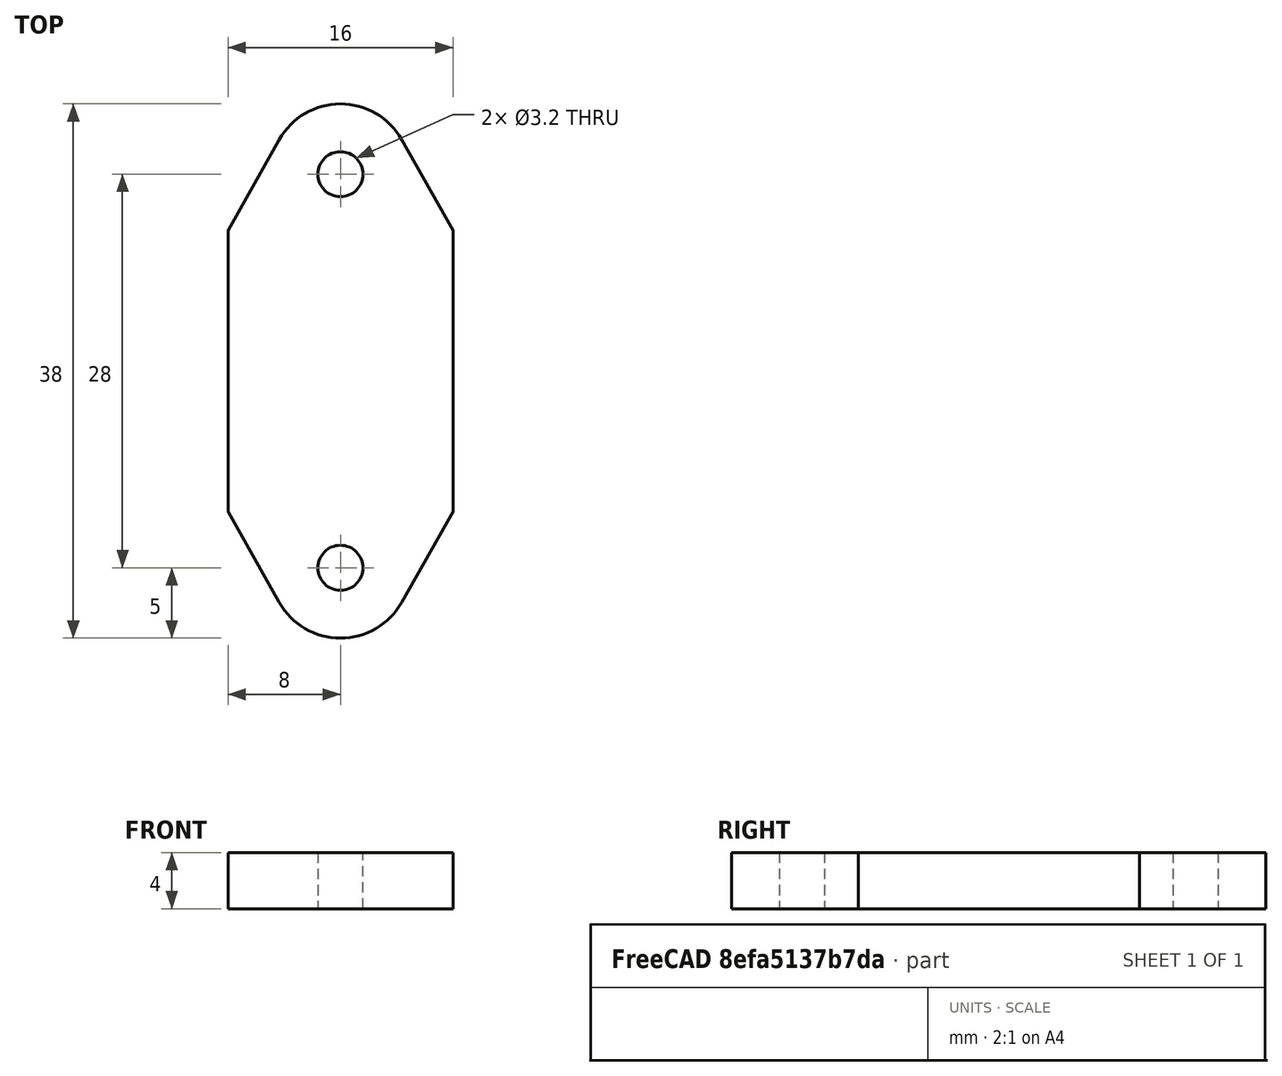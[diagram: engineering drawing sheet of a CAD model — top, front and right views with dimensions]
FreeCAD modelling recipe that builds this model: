
FCSTD DOCUMENT  (FreeCAD 1.0R39285 (Git))
Label: heat spreader
License: All rights reserved
LicenseURL: http://en.wikipedia.org/wiki/All_rights_reserved
objects: Sketcher::SketchObject×1, PartDesign::Pad×1, PartDesign::Body×1
note: 6 computed .brp shape members not serialized (recipe doc carries the construction recipe); baked Part::Feature solids carry a one-line shape summary decoded from their .brp

FEATURE [Sketcher::SketchObject] Sketch
  ArcFitTolerance = 1e-06
  AttachmentSupport = -> [XY_Plane]
  FullyConstrained = true
  MakeInternals = false
  MapMode = 5
  sketch-geometry (14):
    g0: Circle CenterX=0 CenterY=14 CenterZ=0 NormalX=0 NormalY=0 NormalZ=1 AngleXU=0 Radius=1.6
    g1: Circle CenterX=0 CenterY=-14 CenterZ=0 NormalX=0 NormalY=0 NormalZ=1 AngleXU=0 Radius=1.6
    g2: ArcOfCircle CenterX=0 CenterY=14 CenterZ=0 NormalX=0 NormalY=0 NormalZ=1 AngleXU=0 Radius=5 StartAngle=0.513949 EndAngle=2.62764
    g3: ArcOfCircle CenterX=0 CenterY=-14 CenterZ=0 NormalX=0 NormalY=0 NormalZ=1 AngleXU=0 Radius=5 StartAngle=3.65554 EndAngle=5.76924
    g4: LineSegment StartX=-4.35405 StartY=16.4581 StartZ=0 EndX=-8 EndY=10 EndZ=0
    g5: LineSegment StartX=-8 StartY=10 StartZ=0 EndX=-8 EndY=-10 EndZ=0
    g6: LineSegment StartX=-8 StartY=-10 StartZ=0 EndX=-4.35405 EndY=-16.4581 EndZ=0
    g7: LineSegment StartX=4.35405 StartY=-16.4581 StartZ=0 EndX=8 EndY=-10 EndZ=0
    g8: LineSegment StartX=8 StartY=-10 StartZ=0 EndX=8 EndY=10 EndZ=0
    g9: LineSegment StartX=8 StartY=10 StartZ=0 EndX=4.35405 EndY=16.4581 EndZ=0
    g10: LineSegment [constr] StartX=-4.35405 StartY=16.4581 StartZ=0 EndX=4.35405 EndY=16.4581 EndZ=0
    g11: LineSegment [constr] StartX=-8 StartY=10 StartZ=0 EndX=8 EndY=10 EndZ=0
    g12: LineSegment [constr] StartX=-8 StartY=-10 StartZ=0 EndX=8 EndY=-10 EndZ=0
    g13: LineSegment [constr] StartX=-4.35405 StartY=-16.4581 StartZ=0 EndX=4.35405 EndY=-16.4581 EndZ=0
  constraints (34):
    c: PointOnObject(g0,g-2)
    c: Equal(g1,g0)
    c: Radius(g0) = 1.6
    c: DistanceY(g1,g0) = 28
    c: Coincident(g2,g0)
    c: Coincident(g3,g1)
    c: Coincident(g4,g5)
    c: Vertical(g5)
    c: Coincident(g5,g6)
    c: Coincident(g3,g7)
    c: Coincident(g7,g8)
    c: Vertical(g8)
    c: Coincident(g8,g9)
    c: Coincident(g10,g2)
    c: Coincident(g11,g4)
    c: Coincident(g11,g8)
    c: Coincident(g12,g5)
    c: Coincident(g12,g7)
    c: Coincident(g13,g3)
    c: Coincident(g13,g3)
    c: Horizontal(g10)
    c: Horizontal(g11)
    c: Horizontal(g12)
    c: Horizontal(g13)
    c: Equal(g2,g3)
    c: Radius(g2) = 5
    c: Tangent(g2,g4) = -1.5708
    c: Tangent(g9,g2) = -1.5708
    c: Coincident(g10,g2)
    c: DistanceX(g11,g11) = 16
    c: Tangent(g6,g3) = -1.5708
    c: Symmetric(g0,g1,g-1)
    c: DistanceY(g5,g5) = 20
    c: Equal(g4,g6)
FEATURE [PartDesign::Pad] Pad
  Direction = (0,0,1)
  Length = 4
  Length2 = 10
  Profile = -> Sketch
  ReferenceAxis = -> Sketch [N_Axis]
  Refine = true
  Suppressed = false
  Type = 0
FEATURE [PartDesign::Body] Body
  AllowCompound = false
  Group = -> [Sketch,Pad]
  Origin = -> Origin
  Tip = -> Pad
